# Revit family: Display_Mount-Wall-Chief-Kiosk-Portrait
name_source: partatom
category: Specialty Equipment
revit_build: Autodesk Revit 2015 (Build: 20160512_1515(x64)
units: mm (PartAtom-declared; Revit-internal decimal feet)

## types (18) — shared parameters
Date Modified = January 2, 2019
Default Elevation = 48 "
Equipment Abbreviation = VM
Family Version = 1.0
Manufacturer = Chief
Model Disclaimer = Contact Chief For More Information
Product Documentation Link = https://www.legrandav.com
Product Page URL = https://www.legrandav.com
URL = https://www.legrandav.com

## per-type parameters (varying)
| type | Description | Load Capacity | Model | Product Material | z Bezel Height | z Bezel Width | z Type Color | z Type Size |
| 46", Black | Impact™ On-Wall Kiosk Mount, 46 In., Black | 100.000 lb | LW46UBP | Steel - Milestone - Black | 46.5 " | 28.5 " | 0 | 46 |
| 55", Black | Impact™ On-Wall Kiosk Mount, 55 In., Black | 125.000 lb | LW55UBP | Steel - Milestone - Black | 54.5 " | 32.5 " | 0 | 55 |
| 55", White | Impact™ On-Wall Kiosk Mount, 55 In., White | 125.000 lb | LW55UWP | Steel - Milestone - White | 54.5 " | 32.5 " | 1 | 55 |
| 65", Black | Impact™ On-Wall Kiosk Mount, 65 In., Black | 175.000 lb | LW65UBP | Steel - Milestone - Black | 66.5 " | 39.13 " | 0 | 65 |
| 65", White | Impact™ On-Wall Kiosk Mount, 65 In., White | 175.000 lb | LW65UWP | Steel - Milestone - White | 66.5 " | 39.13 " | 1 | 65 |
| 70", Black | Impact™ On-Wall Kiosk Mount, 70 In., Black | 175.000 lb | LW70UBP | Steel - Milestone - Black | 66.5 " | 39.13 " | 0 | 70 |
| 70", White | Impact™ On-Wall Kiosk Mount, 70 In., White | 175.000 lb | LW70UWP | Steel - Milestone - White | 66.5 " | 39.13 " | 1 | 70 |
| 75", Black | Impact™ On-Wall Kiosk Mount, 75 In., Black | 175.000 lb | LW75UBP | Steel - Milestone - Black | 71.5 " | 41.63 " | 0 | 75 |
| 75", White | Impact™ On-Wall Kiosk Mount, 75 In., White | 175.000 lb | LW75UWP | Steel - Milestone - White | 71.5 " | 41.63 " | 1 | 75 |
| 46", White | Impact™ On-Wall Kiosk Mount, 46 In., White | 100.000 lb | LW46UWP | Steel - Milestone - White | 46.5 " | 28.5 " | 1 | 46 |
| 47", Black | Impact™ On-Wall Kiosk Mount, 47 In., Black | 100.000 lb | LW47UBP | Steel - Milestone - Black | 46.5 " | 28.5 " | 0 | 47 |
| 47", White | Impact™ On-Wall Kiosk Mount, 47 In., White | 100.000 lb | LW47UWP | Steel - Milestone - White | 46.5 " | 28.5 " | 1 | 47 |
| 48", Black | Impact™ On-Wall Kiosk Mount, 48 In., Black | 100.000 lb | LW48UBP | Steel - Milestone - Black | 46.5 " | 28.5 " | 0 | 48 |
| 48", White | Impact™ On-Wall Kiosk Mount, 48 In., White | 100.000 lb | LW48UWP | Steel - Milestone - White | 46.5 " | 28.5 " | 1 | 48 |
| 49", Black | Impact™ On-Wall Kiosk Mount, 49 In., Black | 125.000 lb | LW49UBP | Steel - Milestone - Black | 54.5 " | 32.5 " | 0 | 49 |
| 49", White | Impact™ On-Wall Kiosk Mount, 49 In., White | 125.000 lb | LW49UWP | Steel - Milestone - White | 54.5 " | 32.5 " | 1 | 49 |
| 50", Black | Impact™ On-Wall Kiosk Mount, 50 In., Black | 125.000 lb | LW50UBP | Steel - Milestone - Black | 54.5 " | 32.5 " | 0 | 50 |
| 50", White | Impact™ On-Wall Kiosk Mount, 50 In., White | 125.000 lb | LW50UWP | Steel - Milestone - White | 54.5 " | 32.5 " | 1 | 50 |

## geometry (parser evidence)
native form markers: Sweep x5
no freeform markers — native parametric forms only
